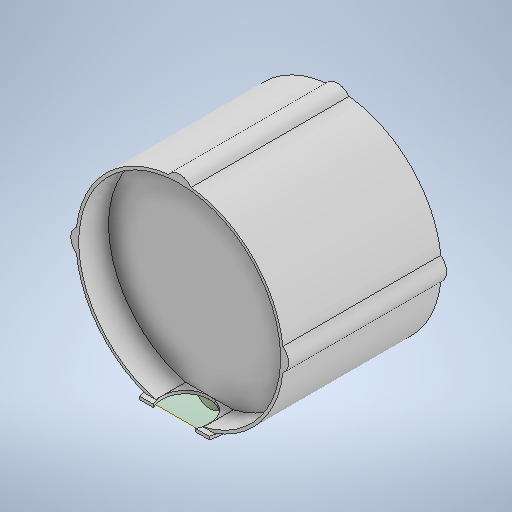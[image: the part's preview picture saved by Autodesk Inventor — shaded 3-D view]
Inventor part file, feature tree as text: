
AUTODESK INVENTOR PART (.ipt)
format: ipt  version: 2025.1 (Build 291241000, 241)  size: 323,072 bytes
history: native  units: mm
features: sketch x5, extrude x4, plane x1
ambient origin geometry x8: Origin, YZ Plane, XZ Plane, XY Plane, X Axis, Y Axis, Z Axis, Center Point
bodies: Solid1 (feature_tree)
feature tree (10):
  extrude  "Extrusion1"  Depth=10.0mm
  extrude  "Extrusion4"  Depth=70.05mm
  extrude  "Extrusion5"  Depth=74.060786mm
  plane  "Arbeitsebene1"
  extrude  "Extrusion6"  Depth=52.9mm TaperAngle=0.0deg
  sketch  "Sketch1"  dims[d0=10.0mm d1=0.25mm]
  sketch  "Skizze - Runde Anordnung1"  dims[d2=40.0mm d4=360.0deg d6=70.05mm]
  sketch  "Skizze4"  dims[d7=0.25mm d8=74.060786mm]
  sketch  "Skizze5"  dims[d9=73.5mm d10=52.9mm d11=0.0mm]
  sketch  "Skizze8"  dims[d24=67.58mm d25=10.0mm d26=0.0mm d27=16.0mm d28=16.0mm d29=35.9mm d30=0.0mm d31=16.0mm d32=1.0mm d33=0.0mm d36=8.0mm]
